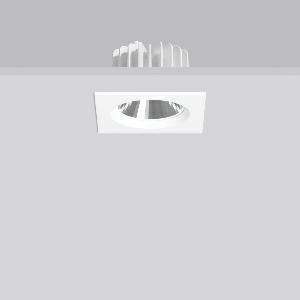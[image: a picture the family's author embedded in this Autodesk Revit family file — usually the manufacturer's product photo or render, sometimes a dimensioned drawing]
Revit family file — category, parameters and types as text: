
# Revit family: ledona_square_ip20_901531_002_2_730_9c84
name_source: partatom
category: Lighting Fixtures
units: mm (PartAtom-declared; Revit-internal decimal feet)

## family parameters
Cut with Voids When Loaded = No
Host = Face
Light Source = No
Part Type = Normal
Room Calculation Point = No
Round Connector Dimension = Use Diameter
Shared = No

## types (1)
- TuneableWhite 846 (1 x LED Modul 846, 1350 lm, 4600)
    Apparent Load = 16 VA
    CIE Flux Codes = 94 100 100 100 100
    Color Rendering = 80
    Color Temperature = 4600
    Default Elevation = 1800 mm
    Description = Series: LEDONA square
Recessed LED downlight featuring advanced technology and sophisticated design. Housing: die-cast aluminium constructed as heat sink. Square cover plate: die-cast aluminium, powder coated. Round ceiling cut-out also with square types. Tunable white dynamically adjustable from 2700 K to 6500 K. Installation without tools thanks to spring fastening system. Connected converter included in separate gearbox. With connecting cable (L 250 mm). With Casambi smart+free Bluetooth control for wireless network and operation using Android / iOS devices, free app available for download. Through-wiring box (5 pole) available as accessory. 
Colour: white
Length: 130 mm
Width: 130 mm
Height: 3 mm
Cut-out diameter: 120 mm
Recess height: 105 mm
Luminaire: recess height: 79 mm
Lamp: LED
Socket: without socket
Colour temperature: 2700K - 6500K
Colour rendering index (CRI): 80
System power: 16 W
Rated luminous flux: 1350 lm
Luminous efficiency: 84 lm/W
System power 2: 16 W
Rated luminous flux 2: 1400 lm
Luminous efficiency 2: 88 lm/W
System power 3: 17 W
Rated luminous flux 3: 1300 lm
Luminous efficiency 3: 76 lm/W
Control gear: Dimmable Bluetooth converter
Protection class: II
Type of protection: IP 20
    Height = 0 mm  [stored 0 ft]
    Lamp = 1 x LED Modul 846
    Lamp Light Flux = 1350 lm
    Lamp count = 1
    Length = 130 mm
    Lifetime = 50000 h
    Luminous efficacy = 84 lm/W
    Manufacturer = RZB
    ModVariant = No
    Model = 901531.002.2.730
    Mounting Place = Ceiling
    Mounting Type = Recessed
    Number of Poles = 1
    OnlyDefault = Yes
    Power Factor = 1
    Product Name = LEDONA square IP20
    Product group = Recessed downlights
    ProductGroupID = 402
    Protection Class = Protection class II
    Protection Degree = IP 20
    RLX_Detail_Level = 1
    RLX_Emergency_Light_Flux = 0 lm
    RLX_Emergency_Type = 0
    RLX_Emergency_Type_DB = No
    RlxData = <blob elided: 31321 chars, md5=635926be>
    Socket = socket
    Standby Power = 0 W
    System Light Flux = 1350 lm
    System Power = 16 W
    Type Comments = TuneableWhite 846
    Type Image = 901389.002.jpg
    URL = http://relux.com
    VarID = tuneablewhite_846
    Voltage = 230 V
    Voltage Range = 220-240 V
    Weight = 0.00 kg
    Width = 130 mm

note: [stored X ft] marks values corroborated as IEEE doubles in the binary element streams (Revit-internal decimal feet)

## geometry (parser evidence)
native form markers: Blend x4, Sweep x10
no freeform markers — native parametric forms only
